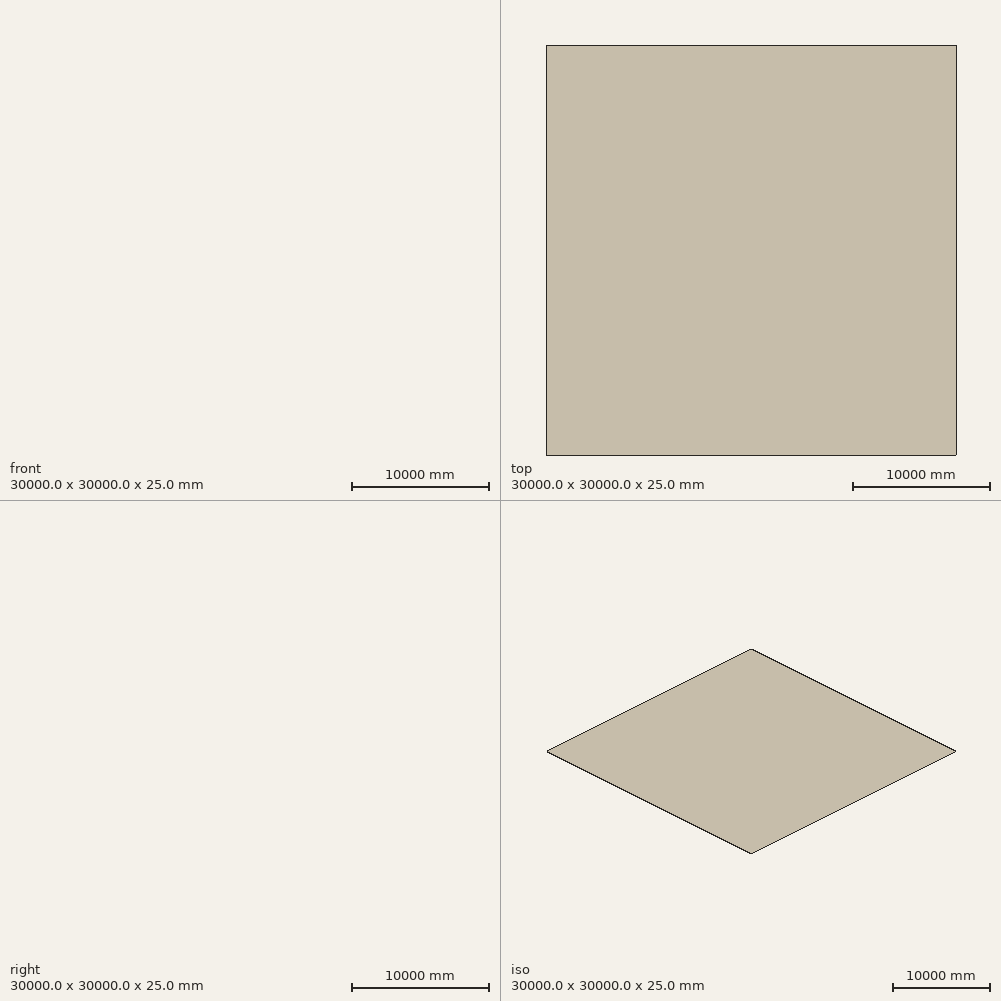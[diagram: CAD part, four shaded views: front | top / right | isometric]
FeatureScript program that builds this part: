
annotation { "Feature Type Name" : "Feature", "Feature Type Description" : "" }
export const myFeature = defineFeature(function(context is Context, id is Id, definition is map)
    precondition{}
    {
        {
            var Q0;
            Q0=qCreatedBy(makeId("Top.planeOp"),FACE);
            var sketch = newSketch(context, id + "F0", { "sketchPlane" : qUnion([Q0])});
            skLineSegment(sketch, "E0.bottom", {"start": v(-15000, 15000) * mm, "end": v(15000, 15000) * mm});
            skLineSegment(sketch, "E0.top", {"start": v(-15000, -15000) * mm, "end": v(15000, -15000) * mm});
            skLineSegment(sketch, "E0.left", {"start": v(-15000, 15000) * mm, "end": v(-15000, -15000) * mm});
            skLineSegment(sketch, "E0.right", {"start": v(15000, 15000) * mm, "end": v(15000, -15000) * mm});
            skSolve(sketch);
        }
        {
            var Q0;
            Q0 = qSketchRegion(id + "F0", true);
            extrude(context, id + "F1", {"entities" : qUnion([Q0]), "depth" : 25 * mm, "offsetDistance" : 25 * mm});
        }
    });
